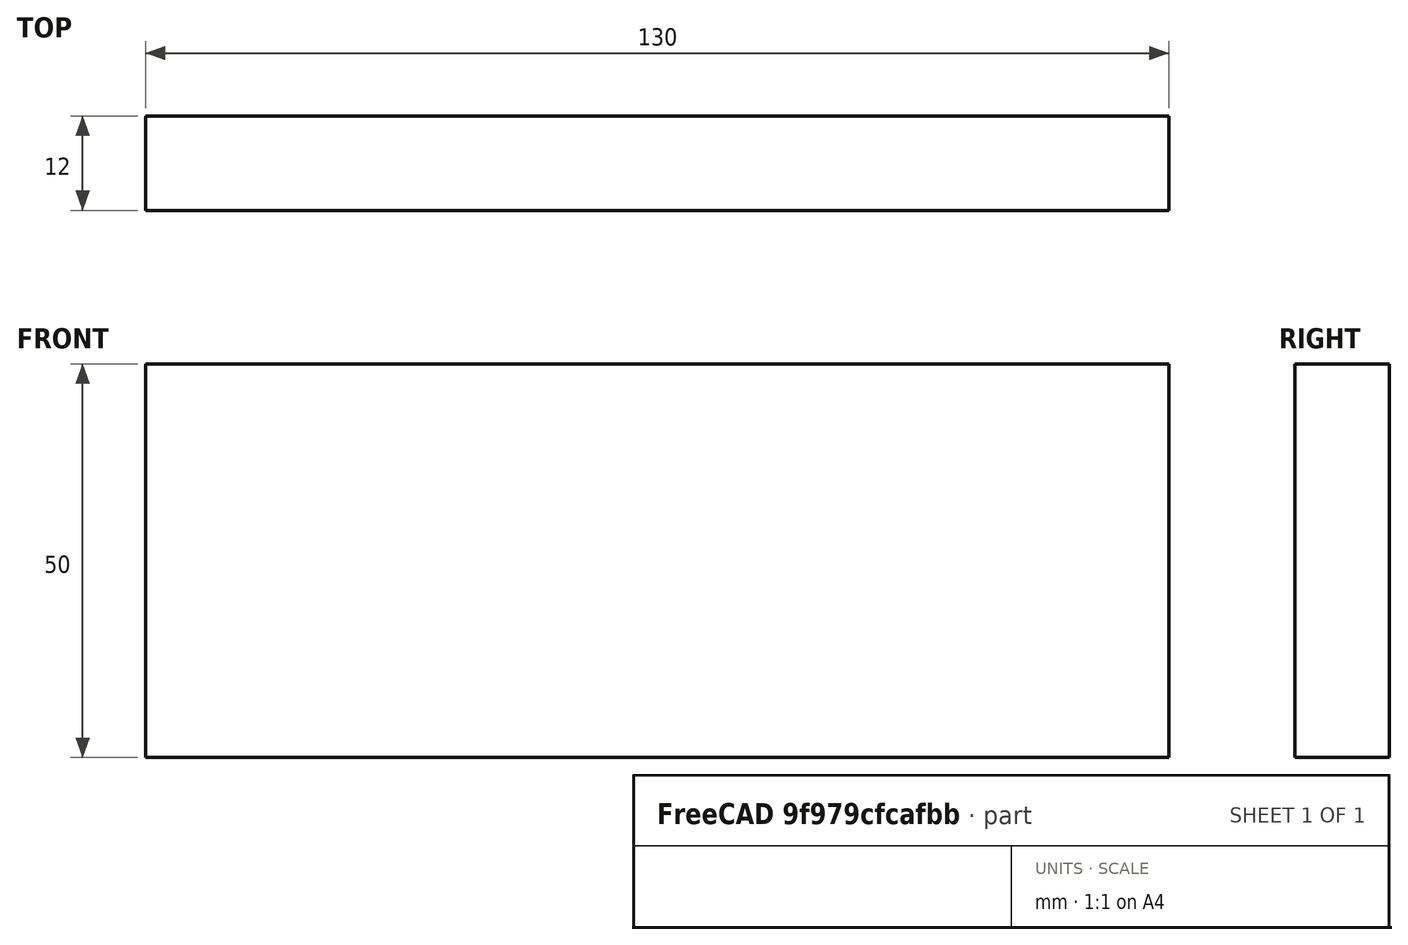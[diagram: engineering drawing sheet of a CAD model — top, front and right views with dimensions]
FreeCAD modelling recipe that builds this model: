
FCSTD DOCUMENT  (FreeCAD 0.15R4671 (Git))
Label: Flat Bar 130x12 EN10058 S235JR
License: All rights reserved
LicenseURL: http://en.wikipedia.org/wiki/All_rights_reserved
objects: Sketcher::SketchObject×1, Part::Extrusion×1
note: 2 computed .brp shape members not serialized (recipe doc carries the construction recipe); baked Part::Feature solids carry a one-line shape summary decoded from their .brp

FEATURE [Sketcher::SketchObject] Sketch
  sketch-geometry (4):
    g0: LineSegment StartX=-65 StartY=-6 StartZ=0 EndX=65 EndY=-6 EndZ=0
    g1: LineSegment StartX=65 StartY=-6 StartZ=0 EndX=65 EndY=6 EndZ=0
    g2: LineSegment StartX=65 StartY=6 StartZ=0 EndX=-65 EndY=6 EndZ=0
    g3: LineSegment StartX=-65 StartY=6 StartZ=0 EndX=-65 EndY=-6 EndZ=0
  constraints (12):
    c: Coincident(g0,g1)
    c: Coincident(g1,g2)
    c: Coincident(g2,g3)
    c: Coincident(g3,g0)
    c: Horizontal(g0)
    c: Horizontal(g2)
    c: Vertical(g1)
    c: Vertical(g3)
    c: Symmetric(g1,g2,g-2)
    c: Symmetric(g0,g1,g-1)
    c: DistanceY(g1) = 12
    c: DistanceX(g0) = 130
FEATURE [Part::Extrusion] Extrude  label="Flat Bar 130x12 EN10058 S235JR"
  Base = -> Sketch
  Dir = (0,0,50)
  Solid = true
